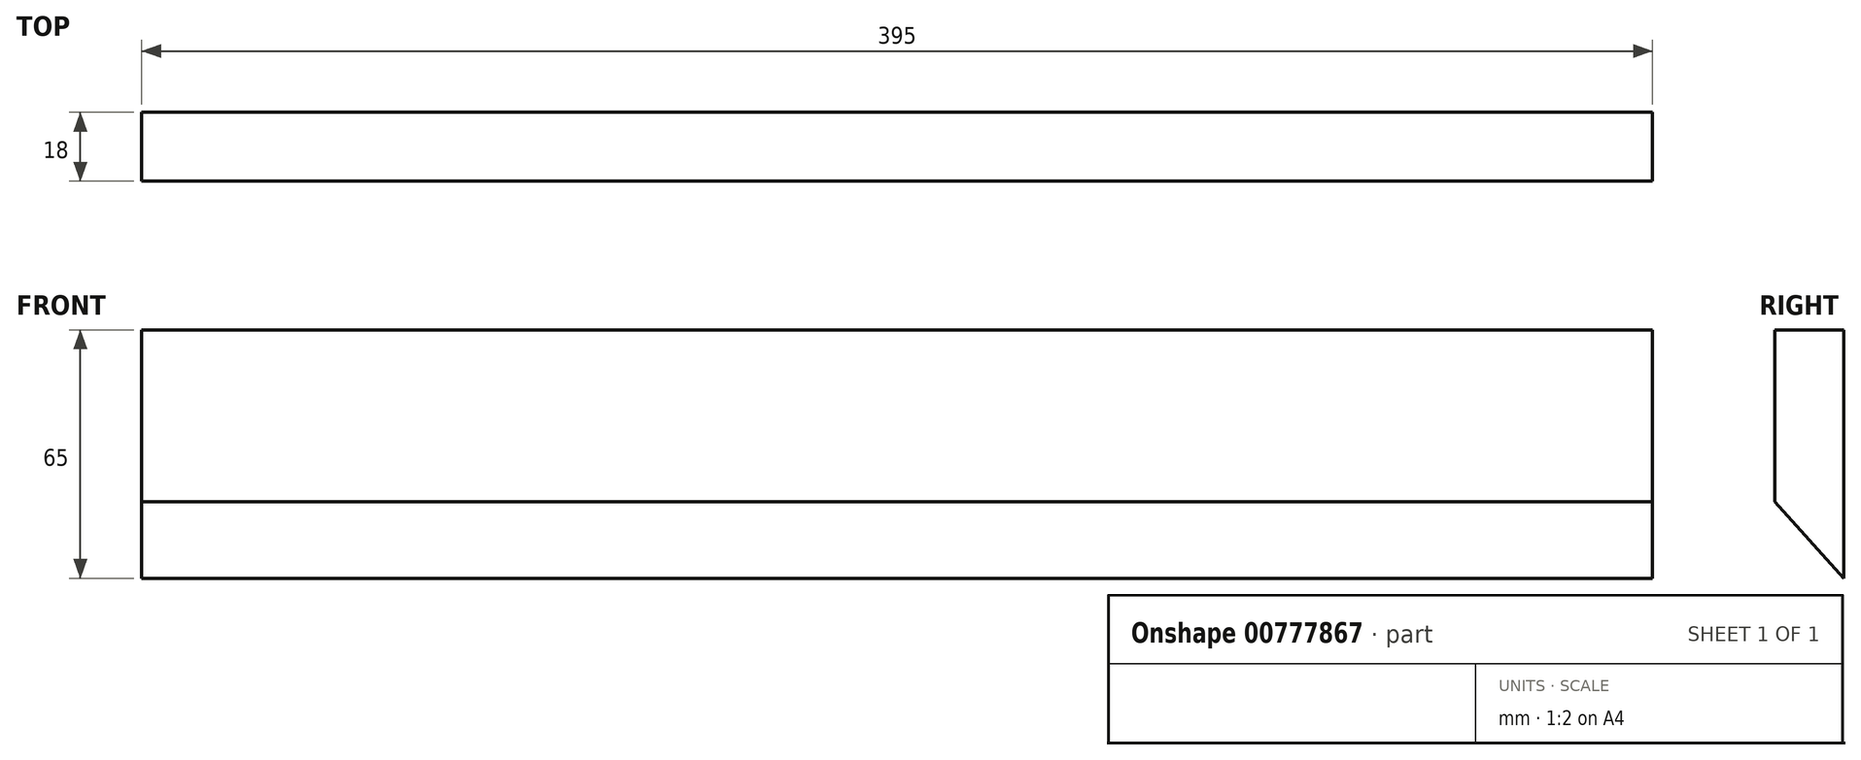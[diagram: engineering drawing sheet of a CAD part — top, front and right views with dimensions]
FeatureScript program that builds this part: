
annotation { "Feature Type Name" : "Feature", "Feature Type Description" : "" }
export const myFeature = defineFeature(function(context is Context, id is Id, definition is map)
    precondition{}
    {
        {
            var Q0;
            Q0=qCreatedBy(makeId("Front.planeOp"),FACE);
            var sketch = newSketch(context, id + "F0", { "sketchPlane" : qUnion([Q0])});
            skLineSegment(sketch, "E0.bottom", {"start": v(-197.5, 32.5) * mm, "end": v(197.5, 32.5) * mm});
            skLineSegment(sketch, "E0.top", {"start": v(-197.5, -32.5) * mm, "end": v(197.5, -32.5) * mm});
            skLineSegment(sketch, "E0.left", {"start": v(-197.5, 32.5) * mm, "end": v(-197.5, -32.5) * mm});
            skLineSegment(sketch, "E0.right", {"start": v(197.5, 32.5) * mm, "end": v(197.5, -32.5) * mm});
            skSolve(sketch);
        }
        {
            var Q0;
            Q0 = qSketchRegion(id + "F0", true);
            extrude(context, id + "F1", {"entities" : qUnion([Q0]), "endBound" : BoundingType.SYMMETRIC, "depth" : 18 * mm, "offsetDistance" : 25 * mm});
        }
        {
            var Q0;
            Q0=makeQuery(id+"F1.opExtrude","SWEPT_FACE",FACE,{"disambiguationData":[OSD([sQuery(id+"F0.wireOp",EDGE,"E0.left")])]});
            var sketch = newSketch(context, id + "F2", { "sketchPlane" : qUnion([Q0])});
            skLineSegment(sketch, "E1", {"start": v(-9, -32.5) * mm, "end": v(9, -12.5) * mm});
            skLineSegment(sketch, "E2", {"start": v(9, -12.5) * mm, "end": v(9, -32.5) * mm});
            skLineSegment(sketch, "E3", {"start": v(9, -32.5) * mm, "end": v(-9, -32.5) * mm});
            skSolve(sketch);
        }
        {
            var Q0;
            Q0 = qSketchRegion(id + "F2", true);
            extrude(context, id + "F3", {"entities" : qUnion([Q0]), "operationType" : NewBodyOperationType.REMOVE, "endBound" : BoundingType.THROUGH_ALL, "oppositeDirection" : true, "depth" : 395 * mm, "offsetDistance" : 25 * mm});
        }
    });
